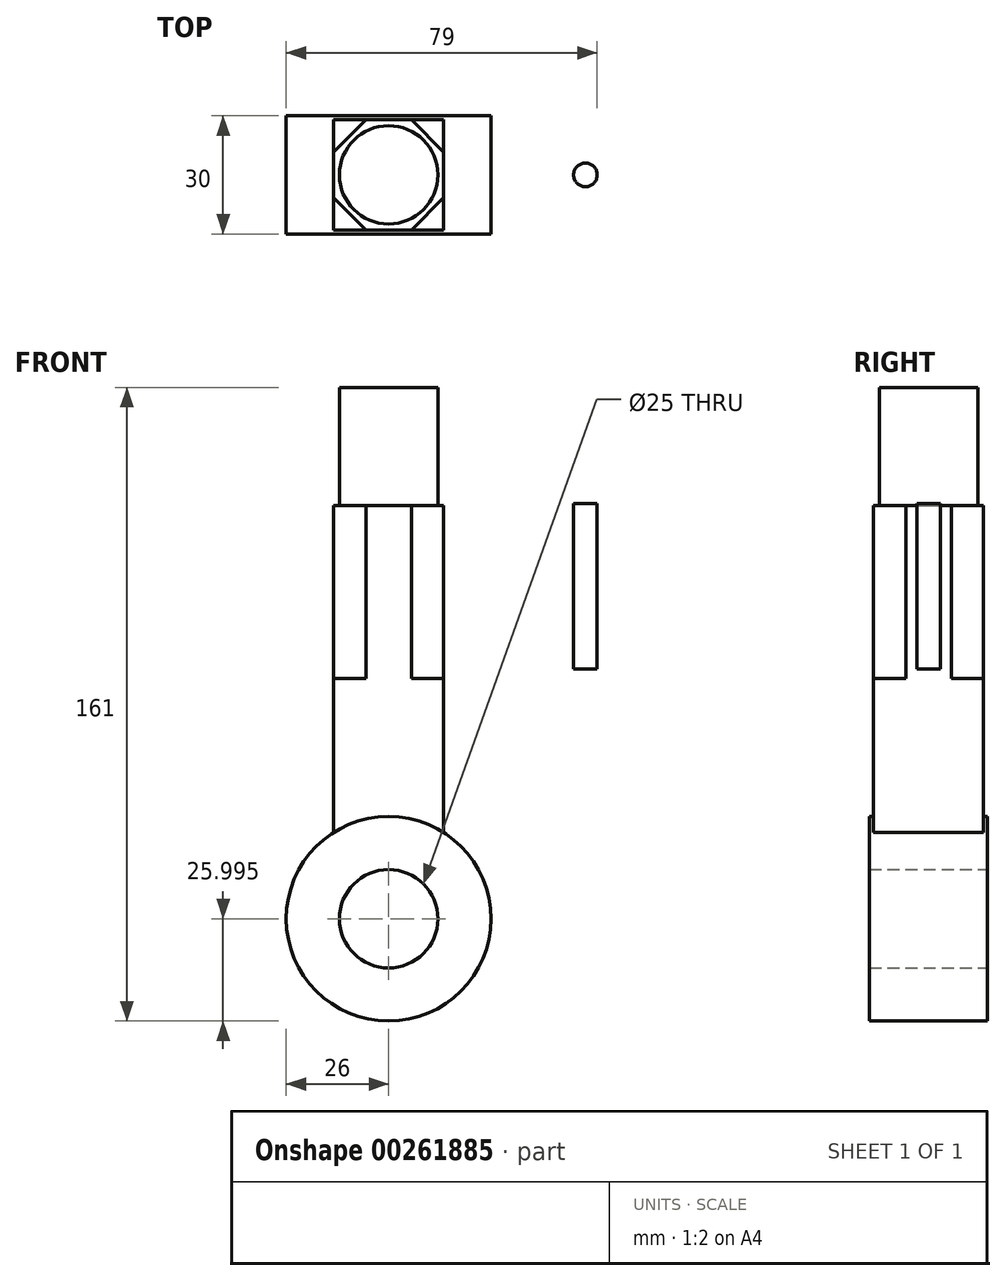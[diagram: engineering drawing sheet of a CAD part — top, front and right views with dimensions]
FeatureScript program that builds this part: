
annotation { "Feature Type Name" : "Feature", "Feature Type Description" : "" }
export const myFeature = defineFeature(function(context is Context, id is Id, definition is map)
    precondition{}
    {
        {
            var Q0;
            Q0=qCreatedBy(makeId("Front.planeOp"),FACE);
            var sketch = newSketch(context, id + "F0", { "sketchPlane" : qUnion([Q0])});
            skLineSegment(sketch, "E0.bottom", {"start": v(14, 41.55) * mm, "end": v(-14, 41.55) * mm});
            skLineSegment(sketch, "E0.top", {"start": v(14, -41.55) * mm, "end": v(-14, -41.55) * mm, "construction": true});
            skLineSegment(sketch, "E0.left", {"start": v(14, 41.55) * mm, "end": v(14, -41.55) * mm});
            skLineSegment(sketch, "E0.right", {"start": v(-14, 41.55) * mm, "end": v(-14, -2.45) * mm, "construction": true});
            skPoint(sketch, "E0.middle", {"position": v(0, 0) * mm});
            skCircle(sketch, "E1", {"center": v(0, -63.45) * mm, "radius": 26 * mm});
            skPoint(sketch, "E1.centerSnap0", {"position": v(0, -41.55) * mm});
            skCircle(sketch, "E2", {"center": v(0, -63.45) * mm, "radius": 12.5 * mm});
            skLineSegment(sketch, "E3", {"start": v(-14, -2.45) * mm, "end": v(14, -2.45) * mm});
            skLineSegment(sketch, "E4", {"start": v(14, -2.45) * mm, "end": v(14, -2.45) * mm});
            skLineSegment(sketch, "E5", {"start": v(-14, -2.45) * mm, "end": v(-14, -41.55) * mm});
            skLineSegment(sketch, "E6", {"start": v(0, 41.55) * mm, "end": v(0, 71.55) * mm});
            skLineSegment(sketch, "E7", {"start": v(0, 71.55) * mm, "end": v(12.5, 71.55) * mm});
            skLineSegment(sketch, "E8", {"start": v(12.5, 71.55) * mm, "end": v(12.5, 41.55) * mm});
            skSolve(sketch);
        }
        {
            var Q0;
            Q0=makeQuery(id+"F0.imprint","IMPRINT",FACE,{"disambiguationData":[TD([[makeQuery(id+"F0.imprint","IMPRINT",EDGE,{"derivedFrom":sQuery(id+"F0.wireOp",EDGE,"E2")}),-1.0]])]});
            extrude(context, id + "F1", {"entities" : qUnion([Q0]), "endBound" : BoundingType.SYMMETRIC, "depth" : 30 * mm});
        }
        {
            var Q0;
            {var subQ3=sQuery(id+"F0.wireOp",EDGE,"E3");Q0=makeQuery(id+"F0.imprint","IMPRINT",FACE,{"disambiguationData":[TD([[makeQuery(id+"F0.imprint","IMPRINT",EDGE,{"derivedFrom":subQ3}),-1.0]])]});}
            extrude(context, id + "F2", {"entities" : qUnion([Q0]), "operationType" : NewBodyOperationType.ADD, "endBound" : BoundingType.SYMMETRIC, "depth" : 28 * mm});
        }
        {
            var Q0;
            Q0=makeQuery(id+"F2.opExtrude","SWEPT_FACE",FACE,{"disambiguationData":[OSD([sQuery(id+"F0.wireOp",EDGE,"E3")])]});
            var sketch = newSketch(context, id + "F3", { "sketchPlane" : qUnion([Q0])});
            skCircle(sketch, "E9.cCircle", {"center": v(0, 0) * mm, "radius": 14 * mm, "construction": true});
            skLineSegment(sketch, "E9.0", {"start": v(5.8, 14) * mm, "end": v(14, 5.8) * mm});
            skLineSegment(sketch, "E9.1", {"start": v(14, 5.8) * mm, "end": v(14, -5.8) * mm});
            skLineSegment(sketch, "E9.2", {"start": v(14, -5.8) * mm, "end": v(5.8, -14) * mm});
            skLineSegment(sketch, "E9.3", {"start": v(5.8, -14) * mm, "end": v(-5.8, -14) * mm});
            skLineSegment(sketch, "E9.4", {"start": v(-5.8, -14) * mm, "end": v(-14, -5.8) * mm});
            skLineSegment(sketch, "E9.5", {"start": v(-14, -5.8) * mm, "end": v(-14, 5.8) * mm});
            skLineSegment(sketch, "E9.6", {"start": v(-14, 5.8) * mm, "end": v(-5.8, 14) * mm});
            skLineSegment(sketch, "E9.7", {"start": v(-5.8, 14) * mm, "end": v(5.8, 14) * mm});
            skPoint(sketch, "E9.0.midPoint", {"position": v(9.9, 9.9) * mm});
            skSolve(sketch);
        }
        {
            var Q0;
            Q0=makeQuery(id+"F3.imprint","IMPRINT",FACE,{"disambiguationData":[TD([[makeQuery(id+"F3.imprint","IMPRINT",EDGE,{"derivedFrom":sQuery(id+"F3.wireOp",EDGE,"E9.0")}),-1.0]])]});
            extrude(context, id + "F4", {"entities" : qUnion([Q0]), "operationType" : NewBodyOperationType.ADD, "depth" : 44 * mm});
        }
        {
            var Q0;
            {var subQ0=sQuery(id+"F0.wireOp",EDGE,"E6");Q0=makeQuery(id+"F0.imprint","IMPRINT",FACE,{"disambiguationData":[TD([[makeQuery(id+"F0.imprint","IMPRINT",EDGE,{"derivedFrom":subQ0}),-1.0]])]});}
            var Q1;
            Q1=sQuery(id+"F0.wireOp",EDGE,"E6");
            revolve(context, id + "F5", {"operationType" : NewBodyOperationType.ADD, "entities" : qUnion([Q0]), "axis" : qUnion([Q1]), "revolveType" : RevolveType.FULL});
        }
        {
            var Q0;
            Q0=qCreatedBy(makeId("Top.planeOp"),FACE);
            var sketch = newSketch(context, id + "F6", { "sketchPlane" : qUnion([Q0])});
            skCircle(sketch, "E10", {"center": v(50, 0) * mm, "radius": 3 * mm});
            skSolve(sketch);
        }
        {
            var Q0;
            Q0 = qSketchRegion(id + "F6", true);
            extrude(context, id + "F7", {"entities" : qUnion([Q0]), "depth" : 42 * mm});
        }
    });
